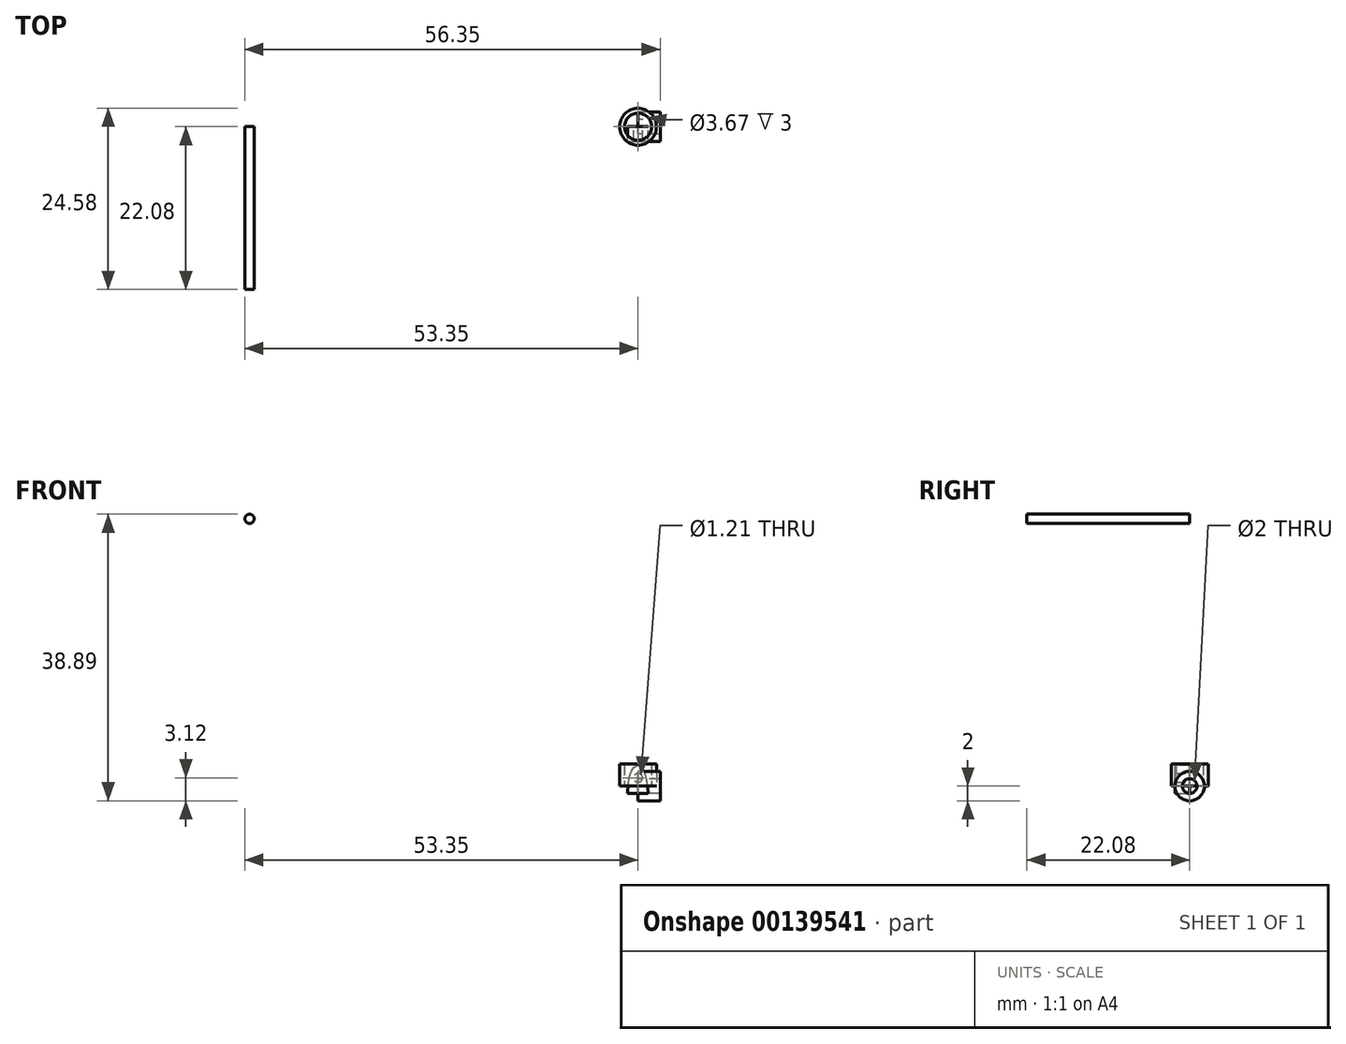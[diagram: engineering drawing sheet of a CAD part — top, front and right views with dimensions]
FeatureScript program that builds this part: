
annotation { "Feature Type Name" : "Feature", "Feature Type Description" : "" }
export const myFeature = defineFeature(function(context is Context, id is Id, definition is map)
    precondition{}
    {
        {
            var Q0;
            Q0=qCreatedBy(makeId("Front.planeOp"),FACE);
            var sketch = newSketch(context, id + "F0", { "sketchPlane" : qUnion([Q0])});
            skCircle(sketch, "E0", {"center": v(-52.72, 36.27) * mm, "radius": 0.63 * mm});
            skSolve(sketch);
        }
        {
            var Q0;
            Q0 = qSketchRegion(id + "F0", true);
            extrude(context, id + "F1", {"entities" : qUnion([Q0]), "depth" : 22.08 * mm});
        }
        {
            var Q0;
            Q0=qCreatedBy(makeId("Top.planeOp"),FACE);
            var sketch = newSketch(context, id + "F2", { "sketchPlane" : qUnion([Q0])});
            skCircle(sketch, "E1", {"center": v(0, 0) * mm, "radius": 2.5 * mm});
            skCircle(sketch, "E2", {"center": v(0, 0) * mm, "radius": 1.83 * mm});
            skSolve(sketch);
        }
        {
            var Q0;
            Q0 = qSketchRegion(id + "F2", true);
            extrude(context, id + "F3", {"entities" : qUnion([Q0]), "depth" : 3 * mm});
        }
        {
            var Q0;
            Q0=qCreatedBy(makeId("Right.planeOp"),FACE);
            var sketch = newSketch(context, id + "F4", { "sketchPlane" : qUnion([Q0])});
            skCircle(sketch, "E3", {"center": v(0, 0) * mm, "radius": 2 * mm});
            skCircle(sketch, "E4", {"center": v(0, 0) * mm, "radius": 1 * mm});
            skSolve(sketch);
        }
        {
            var Q0;
            Q0 = qSketchRegion(id + "F4", true);
            extrude(context, id + "F5", {"entities" : qUnion([Q0]), "depth" : 3 * mm});
        }
        {
            var Q0;
            Q0=qCreatedBy(makeId("Front.planeOp"),FACE);
            var sketch = newSketch(context, id + "F6", { "sketchPlane" : qUnion([Q0])});
            skLineSegment(sketch, "E5.top", {"start": v(-1.4, -1) * mm, "end": v(1.4, -1) * mm});
            skPoint(sketch, "E5.middle", {"position": v(0, 0) * mm});
            skPoint(sketch, "E5.left.start.orphan", {"position": v(-1.4, 1) * mm});
            skPoint(sketch, "E5.right.start.orphan", {"position": v(1.4, 1) * mm});
            skFitSpline(sketch, "E6", {"points": [v(-1.4, -1) * mm, v(0, 2.8) * mm, v(1.4, -1) * mm], "startDerivative": vector(0, 16.56) * mm, "endDerivative": vector(1.92, -16.56) * mm});
            skCircle(sketch, "E7", {"center": v(0, 1.12) * mm, "radius": 0.6 * mm});
            skSolve(sketch);
        }
        {
            var Q0;
            Q0 = qSketchRegion(id + "F6", true);
            extrude(context, id + "F7", {"entities" : qUnion([Q0]), "depth" : 2 * mm});
        }
    });
